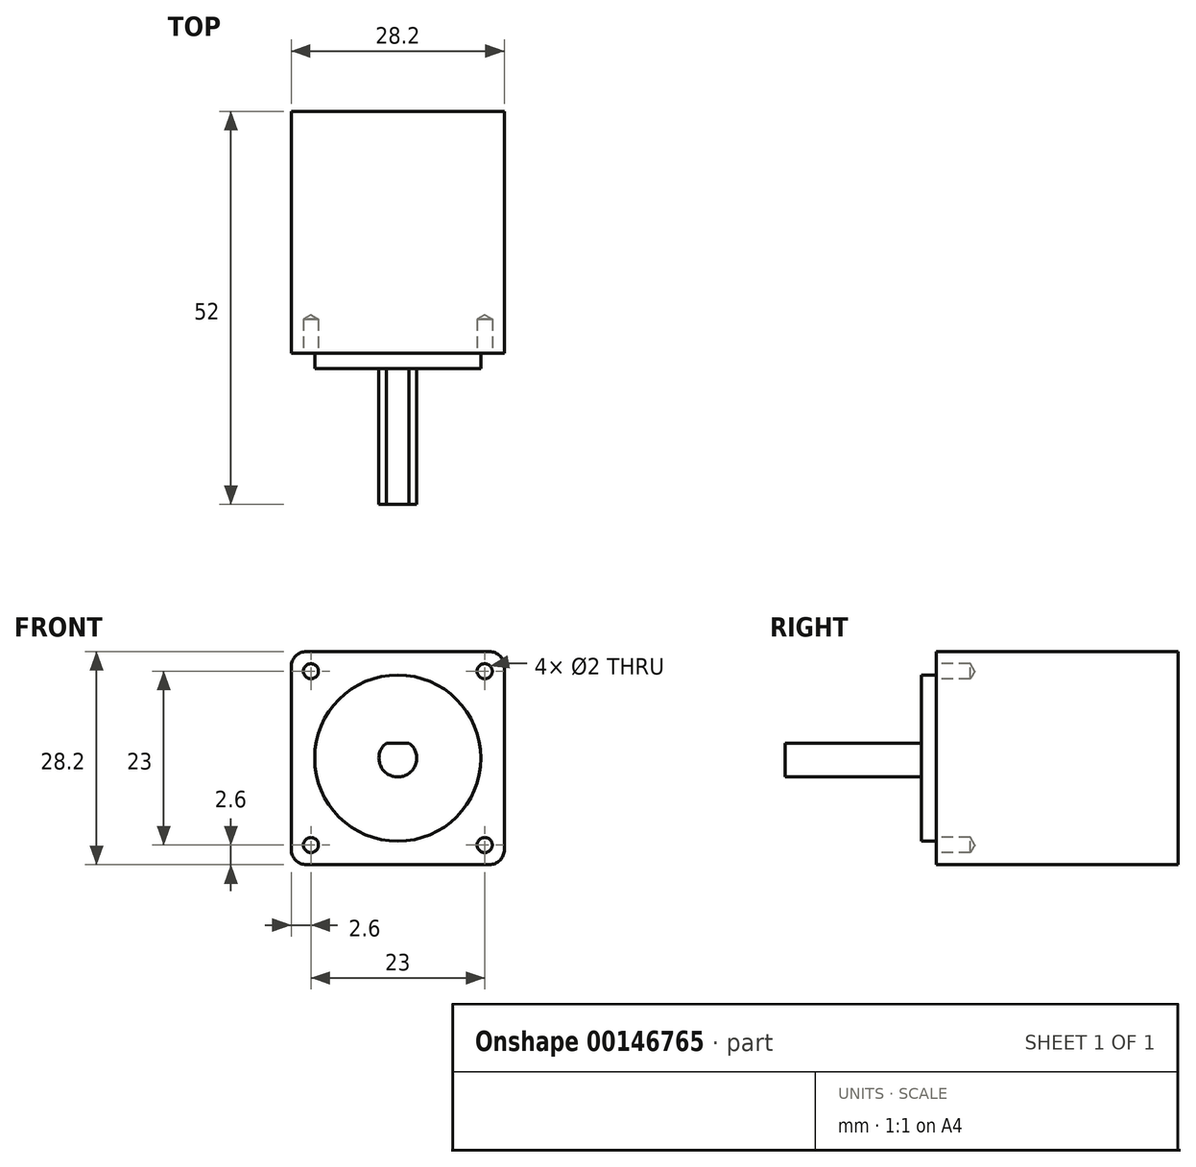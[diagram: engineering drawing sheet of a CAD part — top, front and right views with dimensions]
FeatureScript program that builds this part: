
annotation { "Feature Type Name" : "Feature", "Feature Type Description" : "" }
export const myFeature = defineFeature(function(context is Context, id is Id, definition is map)
    precondition{}
    {
        {
            var Q0;
            Q0=qCreatedBy(makeId("Front.planeOp"),FACE);
            var sketch = newSketch(context, id + "F0", { "sketchPlane" : qUnion([Q0])});
            skLineSegment(sketch, "E0.bottom", {"start": v(14.1, 14.1) * mm, "end": v(-14.1, 14.1) * mm});
            skLineSegment(sketch, "E0.top", {"start": v(14.1, -14.1) * mm, "end": v(-14.1, -14.1) * mm});
            skLineSegment(sketch, "E0.left", {"start": v(14.1, 14.1) * mm, "end": v(14.1, -14.1) * mm});
            skLineSegment(sketch, "E0.right", {"start": v(-14.1, 14.1) * mm, "end": v(-14.1, -14.1) * mm});
            skPoint(sketch, "E0.middle", {"position": v(0, 0) * mm});
            skSolve(sketch);
        }
        {
            var Q0;
            Q0=qSketchRegion(id+"F0",true);
            extrude(context, id + "F1", {"entities" : qUnion([Q0]), "oppositeDirection" : true, "offsetDistance" : 25 * mm, "depth" : 32 * mm});
        }
        {
            var Q0;
            Q0=qCreatedBy(makeId("Front.planeOp"),FACE);
            var sketch = newSketch(context, id + "F2", { "sketchPlane" : qUnion([Q0])});
            skCircle(sketch, "E1", {"center": v(0, 0) * mm, "radius": 11 * mm});
            skSolve(sketch);
        }
        {
            var Q0;
            Q0=qSketchRegion(id+"F2",true);
            extrude(context, id + "F3", {"entities" : qUnion([Q0]), "operationType" : NewBodyOperationType.ADD, "offsetDistance" : 25 * mm, "depth" : 2 * mm});
        }
        {
            var Q0;
            Q0=makeQuery(id+"F3.opExtrude","CAP_FACE",FACE,{"disambiguationData":[OSD([sQuery(id+"F2.wireOp",EDGE,"E1")])],"isStart":false});
            var sketch = newSketch(context, id + "F4", { "sketchPlane" : qUnion([Q0])});
            skArc(sketch, "E2", {"start": v(-1.5, 2) * mm, "mid": v(0, -2.5) * mm, "end": v(1.5, 2) * mm});
            skLineSegment(sketch, "E3", {"start": v(-1.5, 2) * mm, "end": v(1.5, 2) * mm});
            skSolve(sketch);
        }
        {
            var Q0;
            Q0=qSketchRegion(id+"F4",true);
            extrude(context, id + "F5", {"entities" : qUnion([Q0]), "operationType" : NewBodyOperationType.ADD, "offsetDistance" : 25 * mm, "depth" : 18 * mm});
        }
        {
            var Q0;
            Q0=makeQuery(id+"F1.opExtrude","CAP_FACE",FACE,{"disambiguationData":[OSD([sQuery(id+"F0.wireOp",EDGE,"E0.bottom"),sQuery(id+"F0.wireOp",EDGE,"E0.top"),sQuery(id+"F0.wireOp",EDGE,"E0.left"),sQuery(id+"F0.wireOp",EDGE,"E0.right")])],"isStart":true});
            var sketch = newSketch(context, id + "F6", { "sketchPlane" : qUnion([Q0])});
            skLineSegment(sketch, "E4.bottom", {"start": v(11.5, 11.5) * mm, "end": v(-11.5, 11.5) * mm, "construction": true});
            skLineSegment(sketch, "E4.top", {"start": v(11.5, -11.5) * mm, "end": v(-11.5, -11.5) * mm, "construction": true});
            skLineSegment(sketch, "E4.left", {"start": v(11.5, 11.5) * mm, "end": v(11.5, -11.5) * mm, "construction": true});
            skLineSegment(sketch, "E4.right", {"start": v(-11.5, 11.5) * mm, "end": v(-11.5, -11.5) * mm, "construction": true});
            skPoint(sketch, "E4.middle", {"position": v(0, 0) * mm});
            skSolve(sketch);
        }
        {
            var Q0;
            Q0=sQuery(id+"F6.wireOp",VERTEX,"E4.right.start");
            var Q1;
            Q1=sQuery(id+"F6.wireOp",VERTEX,"E4.left.start");
            var Q2;
            Q2=sQuery(id+"F6.wireOp",VERTEX,"E4.left.end");
            var Q3;
            Q3=sQuery(id+"F6.wireOp",VERTEX,"E4.right.end");
            var Q4;
            Q4=makeQuery(id+"F1.opExtrude","SWEPT_BODY",BODY,{"disambiguationData":[OSD([sQuery(id+"F0.wireOp",EDGE,"E0.bottom"),sQuery(id+"F0.wireOp",EDGE,"E0.top"),sQuery(id+"F0.wireOp",EDGE,"E0.left"),sQuery(id+"F0.wireOp",EDGE,"E0.right")])]});
            hole(context, id + "F7", {"style" : HoleStyle.SIMPLE, "endStyle" : HoleEndStyle.BLIND, "holeDiameter" : 2 * mm, "majorDiameter" : 5 * mm, "holeDepth" : 4.5 * mm, "locations" : qUnion([Q0, Q1, Q2, Q3]), "scope" : qUnion([Q4]), "tappedDepth" : 12 * mm, "tapClearance" : 3});
        }
        {
            var Q0;
            Q0=makeQuery(id+"F1.opExtrude","SWEPT_EDGE",EDGE,{"disambiguationData":[OSD([sQuery(id+"F0.wireOp",EDGE,"E0.bottom"),sQuery(id+"F0.wireOp",EDGE,"E0.left")])]});
            var Q1;
            Q1=makeQuery(id+"F1.opExtrude","SWEPT_EDGE",EDGE,{"disambiguationData":[OSD([sQuery(id+"F0.wireOp",EDGE,"E0.top"),sQuery(id+"F0.wireOp",EDGE,"E0.left")])]});
            var Q2;
            Q2=makeQuery(id+"F1.opExtrude","SWEPT_EDGE",EDGE,{"disambiguationData":[OSD([sQuery(id+"F0.wireOp",EDGE,"E0.bottom"),sQuery(id+"F0.wireOp",EDGE,"E0.right")])]});
            var Q3;
            Q3=makeQuery(id+"F1.opExtrude","SWEPT_EDGE",EDGE,{"disambiguationData":[OSD([sQuery(id+"F0.wireOp",EDGE,"E0.top"),sQuery(id+"F0.wireOp",EDGE,"E0.right")])]});
            fillet(context, id + "F8", {"entities" : qUnion([Q0, Q1, Q2, Q3]), "radius" : 2 * mm, "tangentPropagation" : true, "allowEdgeOverflow" : false});
        }
    });
